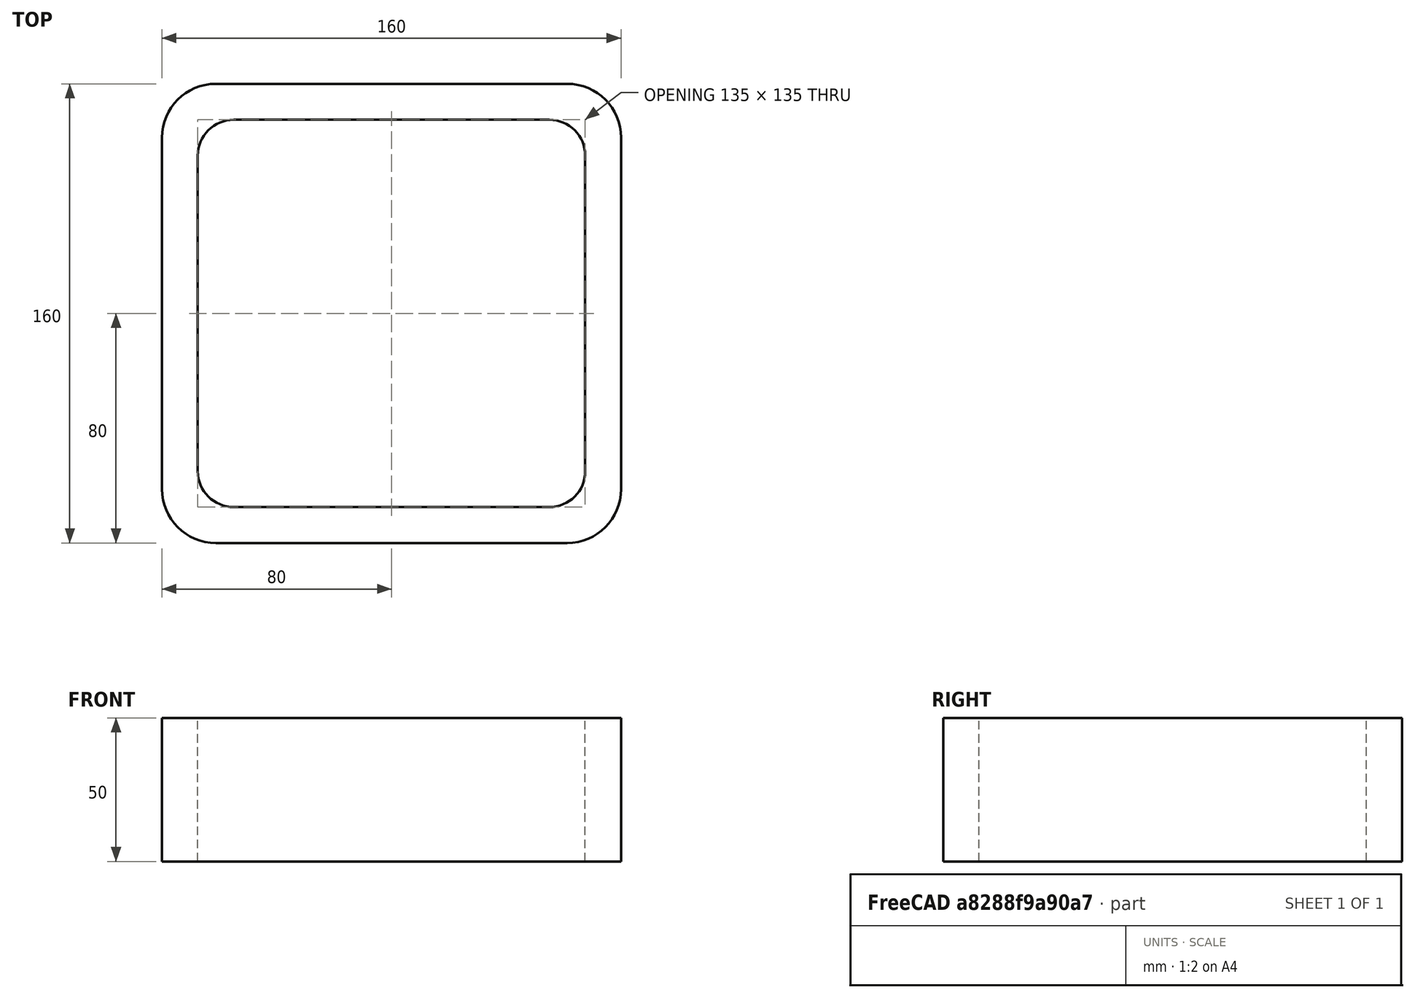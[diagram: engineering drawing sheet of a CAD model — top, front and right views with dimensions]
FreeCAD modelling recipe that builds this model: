
FCSTD DOCUMENT  (FreeCAD 0.15R4671 (Git))
Label: Square hollow section 160x160x12.5 EN10219 S235JRH
License: All rights reserved
LicenseURL: http://en.wikipedia.org/wiki/All_rights_reserved
objects: Sketcher::SketchObject×1, Part::Extrusion×1
note: 2 computed .brp shape members not serialized (recipe doc carries the construction recipe); baked Part::Feature solids carry a one-line shape summary decoded from their .brp

FEATURE [Sketcher::SketchObject] Sketch
  sketch-geometry (16):
    g0: LineSegment StartX=-55 StartY=67.5 StartZ=0 EndX=55 EndY=67.5 EndZ=0
    g1: LineSegment StartX=67.5 StartY=55 StartZ=0 EndX=67.5 EndY=-55 EndZ=0
    g2: LineSegment StartX=55 StartY=-67.5 StartZ=0 EndX=-55 EndY=-67.5 EndZ=0
    g3: LineSegment StartX=-67.5 StartY=-55 StartZ=0 EndX=-67.5 EndY=55 EndZ=0
    g4: LineSegment StartX=-61.25 StartY=80 StartZ=0 EndX=61.25 EndY=80 EndZ=0
    g5: LineSegment StartX=80 StartY=61.25 StartZ=0 EndX=80 EndY=-61.25 EndZ=0
    g6: LineSegment StartX=61.25 StartY=-80 StartZ=0 EndX=-61.25 EndY=-80 EndZ=0
    g7: LineSegment StartX=-80 StartY=-61.25 StartZ=0 EndX=-80 EndY=61.25 EndZ=0
    g8: ArcOfCircle CenterX=-55 CenterY=55 CenterZ=0 NormalX=0 NormalY=0 NormalZ=1 Radius=12.5 StartAngle=1.5708 EndAngle=3.14159
    g9: ArcOfCircle CenterX=55 CenterY=55 CenterZ=0 NormalX=0 NormalY=0 NormalZ=1 Radius=12.5 StartAngle=0 EndAngle=1.5708
    g10: ArcOfCircle CenterX=55 CenterY=-55 CenterZ=0 NormalX=0 NormalY=0 NormalZ=1 Radius=12.5 StartAngle=4.71239 EndAngle=6.28319
    g11: ArcOfCircle CenterX=-55 CenterY=-55 CenterZ=0 NormalX=0 NormalY=0 NormalZ=1 Radius=12.5 StartAngle=3.14159 EndAngle=4.71239
    g12: ArcOfCircle CenterX=61.25 CenterY=61.25 CenterZ=0 NormalX=0 NormalY=0 NormalZ=1 Radius=18.75 StartAngle=0 EndAngle=1.5708
    g13: ArcOfCircle CenterX=61.25 CenterY=-61.25 CenterZ=0 NormalX=0 NormalY=0 NormalZ=1 Radius=18.75 StartAngle=4.71239 EndAngle=6.28319
    g14: ArcOfCircle CenterX=-61.25 CenterY=-61.25 CenterZ=0 NormalX=0 NormalY=0 NormalZ=1 Radius=18.75 StartAngle=3.14159 EndAngle=4.71239
    g15: ArcOfCircle CenterX=-61.25 CenterY=61.25 CenterZ=0 NormalX=0 NormalY=0 NormalZ=1 Radius=18.75 StartAngle=1.5708 EndAngle=3.14159
  constraints (36):
    c: Horizontal(g2)
    c: Vertical(g3)
    c: Horizontal(g6)
    c: Vertical(g7)
    c: Tangent(g3,g8) = 1.5708
    c: Tangent(g0,g8) = 1.5708
    c: Tangent(g0,g9) = 1.5708
    c: Tangent(g1,g9) = 1.5708
    c: Tangent(g1,g10) = 1.5708
    c: Tangent(g2,g10) = 1.5708
    c: Tangent(g2,g11) = 1.5708
    c: Tangent(g3,g11) = 1.5708
    c: Tangent(g4,g12) = 1.5708
    c: Tangent(g5,g12) = 1.5708
    c: Tangent(g5,g13) = 1.5708
    c: Tangent(g6,g13) = 1.5708
    c: Tangent(g6,g14) = 1.5708
    c: Tangent(g7,g14) = 1.5708
    c: Tangent(g7,g15) = 1.5708
    c: Tangent(g4,g15) = 1.5708
    c: Equal(g9,g8)
    c: Equal(g9,g11)
    c: Equal(g9,g10)
    c: Equal(g12,g15)
    c: Equal(g12,g14)
    c: Equal(g12,g13)
    c: Symmetric(g4,g6,g-1)
    c: Symmetric(g7,g5,g-2)
    c: DistanceY(g4,g6) = -160
    c: DistanceX(g7,g5) = 160
    c: Symmetric(g3,g1,g-2)
    c: Symmetric(g0,g2,g-1)
    c: DistanceY(g0,g4) = 12.5
    c: DistanceX(g5,g1) = -12.5
    c: Radius(g9) = 12.5
    c: Radius(g12) = 18.75
FEATURE [Part::Extrusion] Extrude  label="Square hollow section 160x160x12.5 EN10219 S235JRH"
  Base = -> Sketch
  Dir = (0,0,50)
  Solid = true
